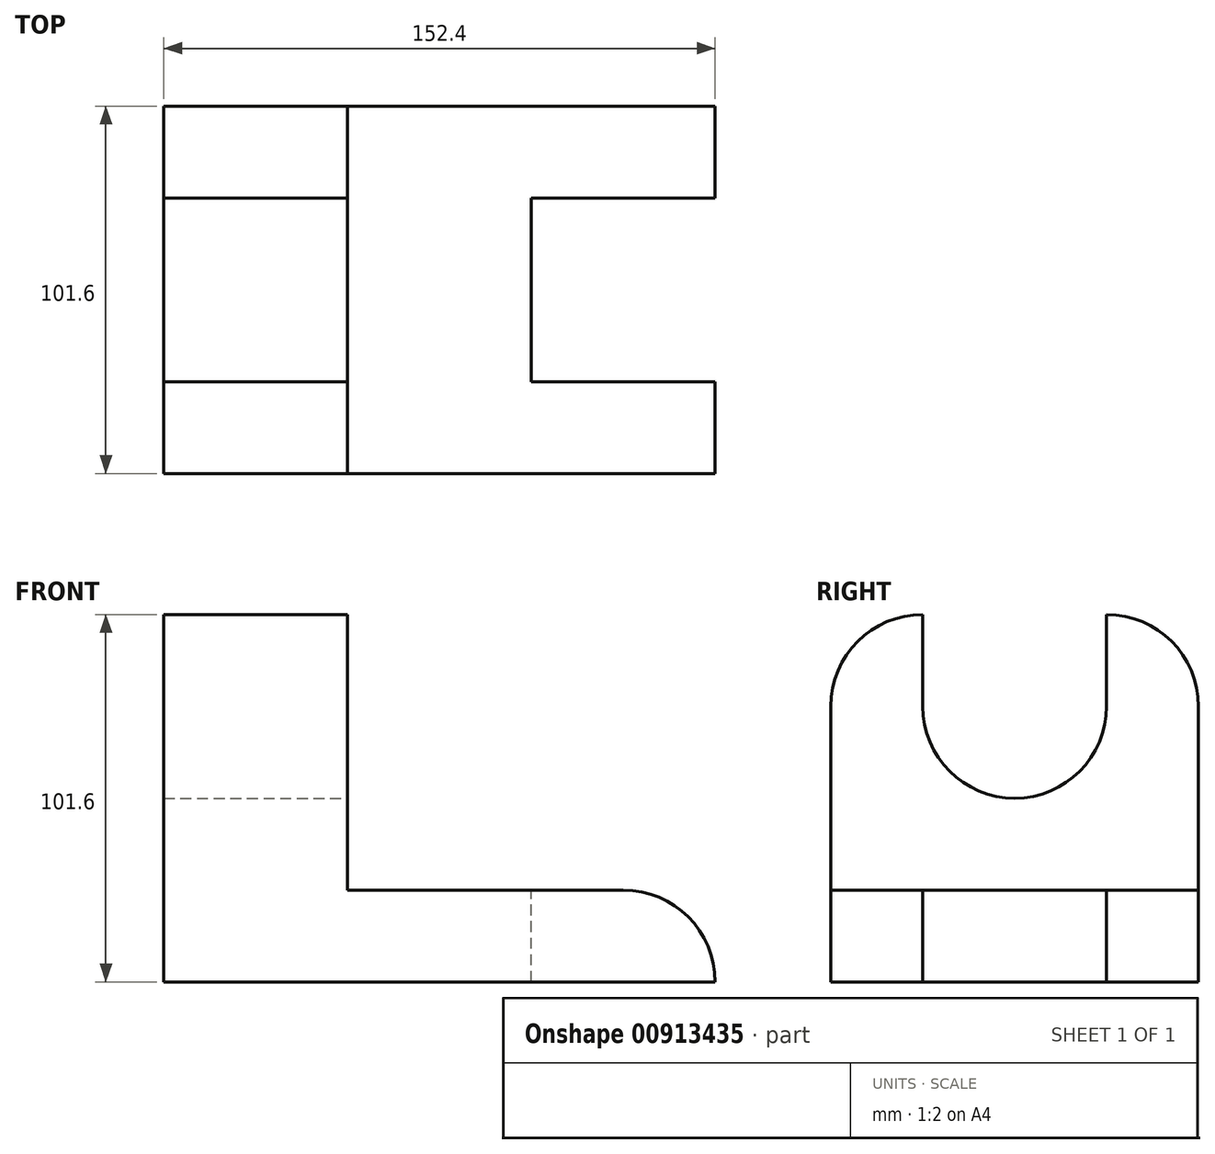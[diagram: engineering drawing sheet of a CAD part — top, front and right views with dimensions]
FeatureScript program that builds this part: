
annotation { "Feature Type Name" : "Feature", "Feature Type Description" : "" }
export const myFeature = defineFeature(function(context is Context, id is Id, definition is map)
    precondition{}
    {
        {
            var Q0;
            Q0=qCreatedBy(makeId("Top.planeOp"),FACE);
            var sketch = newSketch(context, id + "F0", { "sketchPlane" : qUnion([Q0])});
            skLineSegment(sketch, "E0.bottom", {"start": v(0, 0) * mm, "end": v(152.4, 0) * mm});
            skLineSegment(sketch, "E0.top", {"start": v(0, 101.6) * mm, "end": v(152.4, 101.6) * mm});
            skLineSegment(sketch, "E0.left", {"start": v(0, 0) * mm, "end": v(0, 101.6) * mm});
            skLineSegment(sketch, "E0.right", {"start": v(152.4, 0) * mm, "end": v(152.4, 101.6) * mm});
            skSolve(sketch);
        }
        {
            var Q0;
            Q0 = qSketchRegion(id + "F0", true);
            extrude(context, id + "F1", {"entities" : qUnion([Q0]), "depth" : 25.4 * mm, "offsetDistance" : 25.4 * mm});
        }
        {
            var Q0;
            Q0=makeQuery(id+"F1.opExtrude","CAP_FACE",FACE,{"disambiguationData":[OSD([sQuery(id+"F0.wireOp",EDGE,"E0.bottom"),sQuery(id+"F0.wireOp",EDGE,"E0.top"),sQuery(id+"F0.wireOp",EDGE,"E0.left"),sQuery(id+"F0.wireOp",EDGE,"E0.right")])],"isStart":false});
            var sketch = newSketch(context, id + "F2", { "sketchPlane" : qUnion([Q0])});
            skLineSegment(sketch, "E1.bottom", {"start": v(152.4, 76.2) * mm, "end": v(101.6, 76.2) * mm});
            skLineSegment(sketch, "E1.top", {"start": v(152.4, 25.4) * mm, "end": v(101.6, 25.4) * mm});
            skLineSegment(sketch, "E1.left", {"start": v(152.4, 76.2) * mm, "end": v(152.4, 25.4) * mm});
            skLineSegment(sketch, "E1.right", {"start": v(101.6, 76.2) * mm, "end": v(101.6, 25.4) * mm});
            skSolve(sketch);
        }
        {
            var Q0;
            Q0 = qSketchRegion(id + "F2", true);
            extrude(context, id + "F3", {"entities" : qUnion([Q0]), "operationType" : NewBodyOperationType.REMOVE, "endBound" : BoundingType.THROUGH_ALL, "oppositeDirection" : true, "depth" : 25.4 * mm, "offsetDistance" : 25.4 * mm});
        }
        {
            var Q0;
            Q0=makeQuery(id+"F1.opExtrude","CAP_FACE",FACE,{"disambiguationData":[OSD([sQuery(id+"F0.wireOp",EDGE,"E0.bottom"),sQuery(id+"F0.wireOp",EDGE,"E0.top"),sQuery(id+"F0.wireOp",EDGE,"E0.left"),sQuery(id+"F0.wireOp",EDGE,"E0.right")])],"isStart":false});
            var sketch = newSketch(context, id + "F4", { "sketchPlane" : qUnion([Q0])});
            skLineSegment(sketch, "E2.bottom", {"start": v(0, 0) * mm, "end": v(50.8, 0) * mm});
            skLineSegment(sketch, "E2.top", {"start": v(0, 101.6) * mm, "end": v(50.8, 101.6) * mm});
            skLineSegment(sketch, "E2.left", {"start": v(0, 0) * mm, "end": v(0, 101.6) * mm});
            skLineSegment(sketch, "E2.right", {"start": v(50.8, 0) * mm, "end": v(50.8, 101.6) * mm});
            skSolve(sketch);
        }
        {
            var Q0;
            Q0 = qSketchRegion(id + "F4", true);
            extrude(context, id + "F5", {"entities" : qUnion([Q0]), "operationType" : NewBodyOperationType.ADD, "depth" : 76.2 * mm, "offsetDistance" : 25.4 * mm});
        }
        {
            var Q0;
            Q0=makeQuery(id+"F5.opExtrude","SWEPT_FACE",FACE,{"disambiguationData":[OSD([sQuery(id+"F4.wireOp",EDGE,"E2.right")])]});
            var sketch = newSketch(context, id + "F6", { "sketchPlane" : qUnion([Q0])});
            skLineSegment(sketch, "E3.bottom", {"start": v(25.4, 101.6) * mm, "end": v(76.2, 101.6) * mm});
            skLineSegment(sketch, "E3.top", {"start": v(25.4, 76.2) * mm, "end": v(76.2, 76.2) * mm});
            skLineSegment(sketch, "E3.left", {"start": v(25.4, 101.6) * mm, "end": v(25.4, 76.2) * mm});
            skLineSegment(sketch, "E3.right", {"start": v(76.2, 101.6) * mm, "end": v(76.2, 76.2) * mm});
            skSolve(sketch);
        }
        {
            var Q0;
            Q0 = qSketchRegion(id + "F6", true);
            extrude(context, id + "F7", {"entities" : qUnion([Q0]), "operationType" : NewBodyOperationType.REMOVE, "endBound" : BoundingType.THROUGH_ALL, "oppositeDirection" : true, "depth" : 25.4 * mm, "offsetDistance" : 25.4 * mm});
        }
        {
            var Q0;
            Q0=makeQuery(id+"F5.opExtrude","SWEPT_FACE",FACE,{"disambiguationData":[OSD([sQuery(id+"F4.wireOp",EDGE,"E2.right")])]});
            var sketch = newSketch(context, id + "F8", { "sketchPlane" : qUnion([Q0])});
            skArc(sketch, "E4", {"start": v(25.4, 76.2) * mm, "mid": v(50.8, 50.8) * mm, "end": v(76.2, 76.2) * mm});
            skSolve(sketch);
        }
        {
            var Q0;
            Q0 = qSketchRegion(id + "F8", true);
            var Q1;
            Q1=makeQuery(id+"F8.imprint","IMPRINT",FACE,{"disambiguationData":[TD([[makeQuery(id+"F8.imprint","IMPRINT",EDGE,{"derivedFrom":sQuery(id+"F8.wireOp",EDGE,"E4")}),1.0]])]});
            extrude(context, id + "F9", {"entities" : qUnion([Q0, Q1]), "operationType" : NewBodyOperationType.REMOVE, "endBound" : BoundingType.THROUGH_ALL, "oppositeDirection" : true, "depth" : 25.4 * mm, "offsetDistance" : 25.4 * mm});
        }
        {
            var Q0;
            Q0=makeQuery(id+"F5.opExtrude","CAP_EDGE",EDGE,{"disambiguationData":[OSD([sQuery(id+"F4.wireOp",EDGE,"E2.bottom")])],"isStart":false});
            var Q1;
            Q1=makeQuery(id+"F5.opExtrude","CAP_EDGE",EDGE,{"disambiguationData":[OSD([sQuery(id+"F4.wireOp",EDGE,"E2.top")])],"isStart":false});
            var Q2;
            {var subQ0=sQuery(id+"F0.wireOp",EDGE,"E0.bottom");var subQ1=sQuery(id+"F0.wireOp",EDGE,"E0.right");Q2=makeQuery(id+"F3.boolean.opBoolean","SPLIT",EDGE,{"disambiguationData":[TD([makeQuery(id+"F1.opExtrude","SWEPT_FACE",FACE,{"disambiguationData":[OSD([subQ0])]})])],"derivedFrom":makeQuery(id+"F1.opExtrude","CAP_EDGE",EDGE,{"disambiguationData":[OSD([subQ1])],"isStart":false})});}
            var Q3;
            {var subQ0=sQuery(id+"F0.wireOp",EDGE,"E0.right");var subQ1=sQuery(id+"F0.wireOp",EDGE,"E0.top");Q3=makeQuery(id+"F3.boolean.opBoolean","SPLIT",EDGE,{"disambiguationData":[TD([makeQuery(id+"F1.opExtrude","SWEPT_FACE",FACE,{"disambiguationData":[OSD([subQ1])]})])],"derivedFrom":makeQuery(id+"F1.opExtrude","CAP_EDGE",EDGE,{"disambiguationData":[OSD([subQ0])],"isStart":false})});}
            fillet(context, id + "F10", {"entities" : qUnion([Q0, Q1, Q2, Q3]), "radius" : 25.4 * mm, "tangentPropagation" : true, "allowEdgeOverflow" : false});
        }
    });
